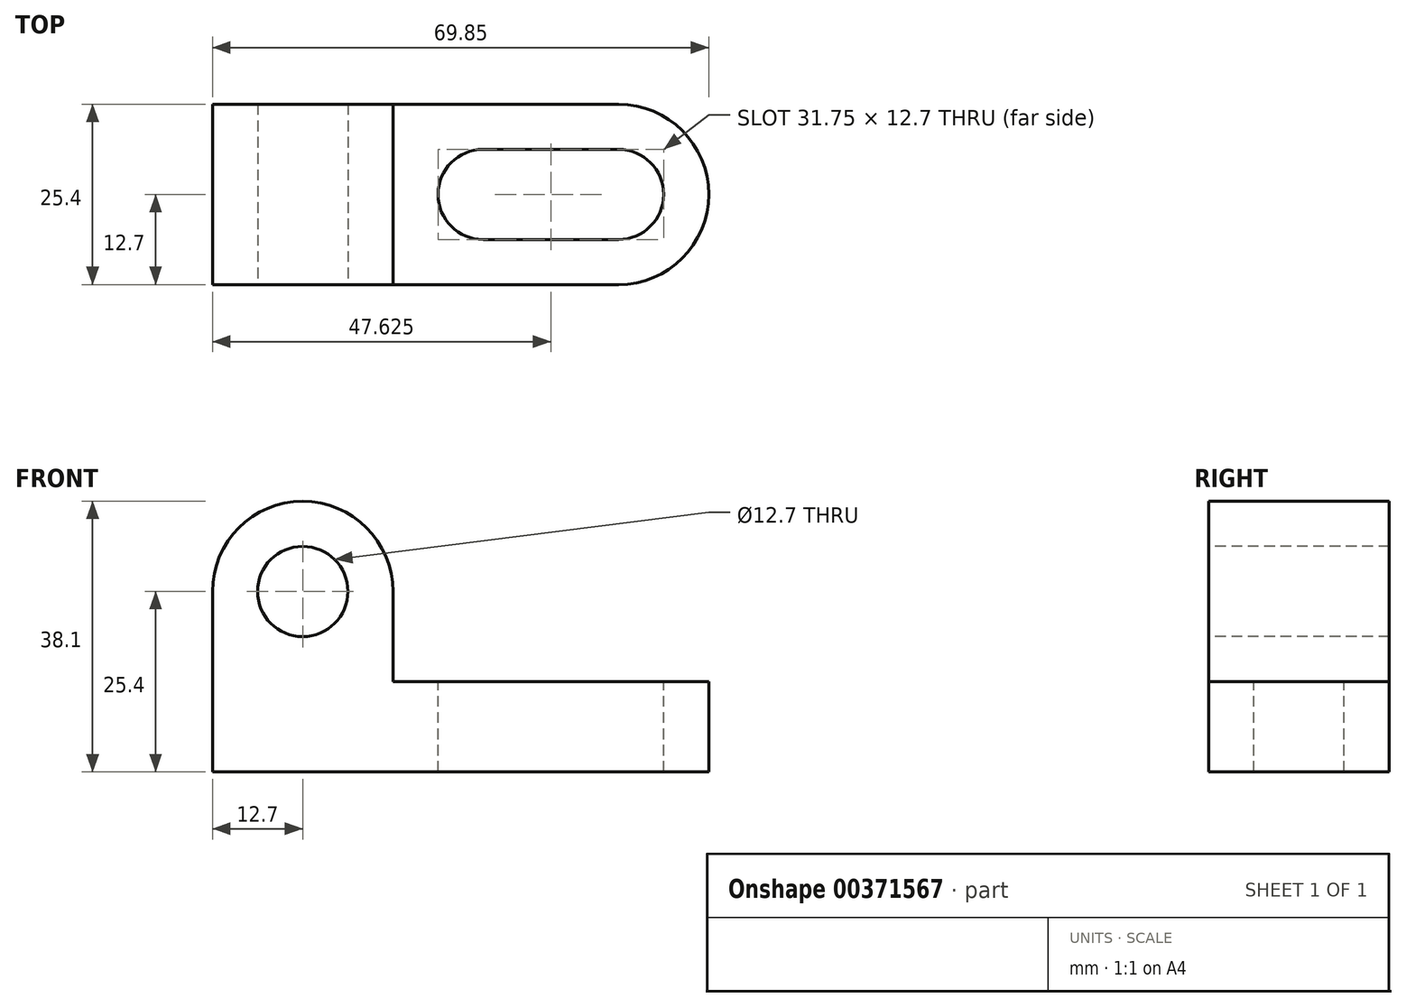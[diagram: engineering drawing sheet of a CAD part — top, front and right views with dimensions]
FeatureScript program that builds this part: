
annotation { "Feature Type Name" : "Feature", "Feature Type Description" : "" }
export const myFeature = defineFeature(function(context is Context, id is Id, definition is map)
    precondition{}
    {
        {
            var Q0;
            Q0=qCreatedBy(makeId("Front.planeOp"),FACE);
            var sketch = newSketch(context, id + "F0", { "sketchPlane" : qUnion([Q0])});
            skLineSegment(sketch, "E0", {"start": v(0, 0) * mm, "end": v(0, 38.1) * mm});
            skLineSegment(sketch, "E1", {"start": v(0, 38.1) * mm, "end": v(25.4, 38.1) * mm});
            skLineSegment(sketch, "E2", {"start": v(25.4, 38.1) * mm, "end": v(25.4, 12.7) * mm});
            skLineSegment(sketch, "E3", {"start": v(25.4, 12.7) * mm, "end": v(69.85, 12.7) * mm});
            skLineSegment(sketch, "E4", {"start": v(69.85, 12.7) * mm, "end": v(69.85, 0) * mm});
            skLineSegment(sketch, "E5", {"start": v(69.85, 0) * mm, "end": v(0, 0) * mm});
            skSolve(sketch);
        }
        {
            var Q0;
            Q0=makeQuery(id+"F0.imprint","IMPRINT",FACE,{"disambiguationData":[TD([[makeQuery(id+"F0.imprint","IMPRINT",EDGE,{"derivedFrom":sQuery(id+"F0.wireOp",EDGE,"E0")}),-1.0]])]});
            extrude(context, id + "F1", {"entities" : qUnion([Q0]), "depth" : 25.4 * mm});
        }
        {
            var Q0;
            Q0=makeQuery(id+"F1.opExtrude","CAP_FACE",FACE,{"disambiguationData":[OSD([sQuery(id+"F0.wireOp",EDGE,"E0"),sQuery(id+"F0.wireOp",EDGE,"E1"),sQuery(id+"F0.wireOp",EDGE,"E2"),sQuery(id+"F0.wireOp",EDGE,"E3"),sQuery(id+"F0.wireOp",EDGE,"E4"),sQuery(id+"F0.wireOp",EDGE,"E5")])],"isStart":false});
            var sketch = newSketch(context, id + "F2", { "sketchPlane" : qUnion([Q0])});
            skCircle(sketch, "E6", {"center": v(12.7, 25.4) * mm, "radius": 6.35 * mm});
            skPoint(sketch, "E6.centerSnap0", {"position": v(12.7, 38.1) * mm});
            skArc(sketch, "E7", {"start": v(25.4, 25.4) * mm, "mid": v(12.7, 38.1) * mm, "end": v(0, 25.4) * mm});
            skSolve(sketch);
        }
        {
            var Q0;
            Q0=makeQuery(id+"F2.imprint","IMPRINT",FACE,{"disambiguationData":[TD([[makeQuery(id+"F2.imprint","IMPRINT",EDGE,{"derivedFrom":sQuery(id+"F2.wireOp",EDGE,"E6")}),1.0]])]});
            extrude(context, id + "F3", {"entities" : qUnion([Q0]), "operationType" : NewBodyOperationType.REMOVE, "oppositeDirection" : true, "depth" : 25.4 * mm});
        }
        {
            var Q0;
            Q0 = qSketchRegion(id + "F2", true);
            var Q1;
            {var subQ0=sQuery(id+"F2.wireOp",EDGE,"E7");var subQ1=makeQuery(id+"F1.opExtrude","CAP_EDGE",EDGE,{"disambiguationData":[OSD([sQuery(id+"F0.wireOp",EDGE,"E0")])],"isStart":false});var subQ2=makeQuery(id+"F2.imprint","INTERSECT",VERTEX,{"derivedFrom":[subQ1,subQ0]});Q1=makeQuery(id+"F2.imprint","IMPRINT",FACE,{"disambiguationData":[TD([[makeQuery(id+"F2.imprint","IMPRINT",EDGE,{"disambiguationData":[TD([[subQ2,1.0]])],"derivedFrom":subQ0}),-1.0]])]});}
            var Q2;
            {var subQ0=sQuery(id+"F2.wireOp",EDGE,"E7");var subQ1=makeQuery(id+"F1.opExtrude","CAP_EDGE",EDGE,{"disambiguationData":[OSD([sQuery(id+"F0.wireOp",EDGE,"E2")])],"isStart":false});var subQ2=makeQuery(id+"F2.imprint","INTERSECT",VERTEX,{"derivedFrom":[subQ1,subQ0]});Q2=makeQuery(id+"F2.imprint","IMPRINT",FACE,{"disambiguationData":[TD([[makeQuery(id+"F2.imprint","IMPRINT",EDGE,{"disambiguationData":[TD([[subQ2,-1.0]])],"derivedFrom":subQ0}),-1.0]])]});}
            extrude(context, id + "F4", {"entities" : qUnion([Q0, Q1, Q2]), "operationType" : NewBodyOperationType.REMOVE, "oppositeDirection" : true, "depth" : 25.4 * mm});
        }
        {
            var Q0;
            Q0=makeQuery(id+"F1.opExtrude","SWEPT_FACE",FACE,{"disambiguationData":[OSD([sQuery(id+"F0.wireOp",EDGE,"E3")])]});
            var sketch = newSketch(context, id + "F5", { "sketchPlane" : qUnion([Q0])});
            skCircle(sketch, "E8", {"center": v(38.1, -12.7) * mm, "radius": 6.35 * mm});
            skCircle(sketch, "E9", {"center": v(57.15, -12.7) * mm, "radius": 6.35 * mm});
            skLineSegment(sketch, "E10", {"start": v(38.1, -6.35) * mm, "end": v(57.15, -6.35) * mm});
            skLineSegment(sketch, "E11", {"start": v(38.1, -19.05) * mm, "end": v(57.15, -19.05) * mm});
            skPoint(sketch, "E12.end.orphan", {"position": v(57.15, 0) * mm});
            skPoint(sketch, "E12.start.orphan", {"position": v(57.15, -25.4) * mm});
            skArc(sketch, "E13", {"start": v(57.15, -25.4) * mm, "mid": v(69.85, -12.7) * mm, "end": v(57.15, 0) * mm});
            skSolve(sketch);
        }
        {
            var Q0;
            {var subQ0=sQuery(id+"F5.wireOp",EDGE,"E8");var subQ1=makeQuery(id+"F5.imprint","INTERSECT",VERTEX,{"derivedFrom":[subQ0,sQuery(id+"F5.wireOp",EDGE,"E10")]});Q0=makeQuery(id+"F5.imprint","IMPRINT",FACE,{"disambiguationData":[TD([[makeQuery(id+"F5.imprint","IMPRINT",EDGE,{"disambiguationData":[TD([[subQ1,-1.0]])],"derivedFrom":subQ0}),1.0]])]});}
            var Q1;
            {var subQ0=sQuery(id+"F5.wireOp",EDGE,"E10");Q1=makeQuery(id+"F5.imprint","IMPRINT",FACE,{"disambiguationData":[TD([[makeQuery(id+"F5.imprint","IMPRINT",EDGE,{"derivedFrom":subQ0}),-1.0]])]});}
            var Q2;
            {var subQ0=sQuery(id+"F5.wireOp",EDGE,"E9");var subQ1=makeQuery(id+"F5.imprint","INTERSECT",VERTEX,{"derivedFrom":[subQ0,sQuery(id+"F5.wireOp",EDGE,"E10")]});Q2=makeQuery(id+"F5.imprint","IMPRINT",FACE,{"disambiguationData":[TD([[makeQuery(id+"F5.imprint","IMPRINT",EDGE,{"disambiguationData":[TD([[subQ1,-1.0]])],"derivedFrom":subQ0}),1.0]])]});}
            var Q3;
            {var subQ0=sQuery(id+"F5.wireOp",EDGE,"E13");var subQ1=sQuery(id+"F0.wireOp",EDGE,"E3");var subQ2=makeQuery(id+"F1.opExtrude","CAP_EDGE",EDGE,{"disambiguationData":[OSD([subQ1])],"isStart":true});var subQ3=makeQuery(id+"F5.imprint","INTERSECT",VERTEX,{"derivedFrom":[subQ2,subQ0]});Q3=makeQuery(id+"F5.imprint","IMPRINT",FACE,{"disambiguationData":[TD([[makeQuery(id+"F5.imprint","IMPRINT",EDGE,{"disambiguationData":[TD([[subQ3,1.0]])],"derivedFrom":subQ0}),-1.0]])]});}
            var Q4;
            {var subQ0=sQuery(id+"F5.wireOp",EDGE,"E13");var subQ1=sQuery(id+"F0.wireOp",EDGE,"E3");var subQ2=makeQuery(id+"F1.opExtrude","CAP_EDGE",EDGE,{"disambiguationData":[OSD([subQ1])],"isStart":false});var subQ3=makeQuery(id+"F5.imprint","INTERSECT",VERTEX,{"derivedFrom":[subQ2,subQ0]});Q4=makeQuery(id+"F5.imprint","IMPRINT",FACE,{"disambiguationData":[TD([[makeQuery(id+"F5.imprint","IMPRINT",EDGE,{"disambiguationData":[TD([[subQ3,-1.0]])],"derivedFrom":subQ0}),-1.0]])]});}
            extrude(context, id + "F6", {"entities" : qUnion([Q0, Q1, Q2, Q3, Q4]), "operationType" : NewBodyOperationType.REMOVE, "oppositeDirection" : true, "depth" : 25.4 * mm});
        }
    });
